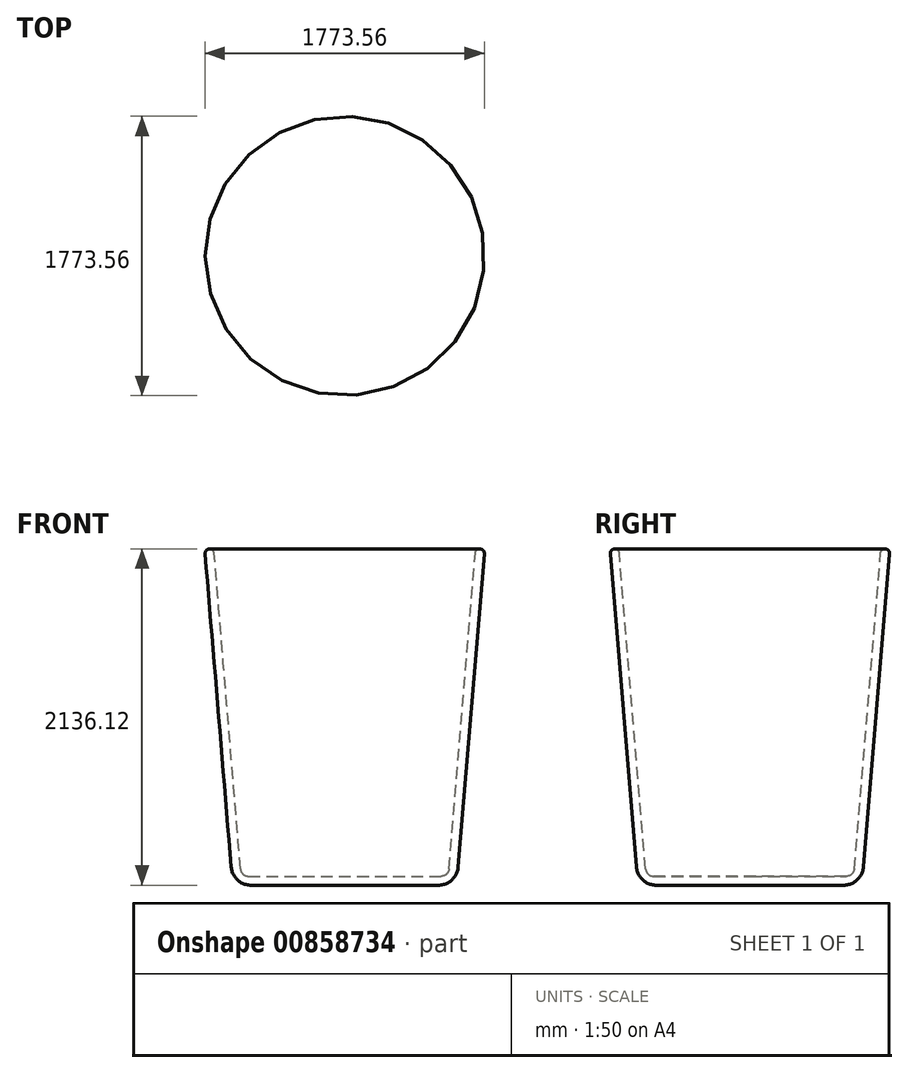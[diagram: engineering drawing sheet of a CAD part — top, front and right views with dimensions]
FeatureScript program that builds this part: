
annotation { "Feature Type Name" : "Feature", "Feature Type Description" : "" }
export const myFeature = defineFeature(function(context is Context, id is Id, definition is map)
    precondition{}
    {
        {
            var Q0;
            Q0=qCreatedBy(makeId("Front.planeOp"),FACE);
            var sketch = newSketch(context, id + "F0", { "sketchPlane" : qUnion([Q0])});
            skLineSegment(sketch, "E0", {"start": v(116.86, 0) * mm, "end": v(711.2, 0) * mm});
            skLineSegment(sketch, "E1", {"start": v(-9.7, 116.45) * mm, "end": v(-175.48, 2105.76) * mm});
            skLineSegment(sketch, "E2", {"start": v(711.2, 0) * mm, "end": v(711.2, 2133.6) * mm});
            skLineSegment(sketch, "E3.0", {"start": v(48.7, 103.73) * mm, "end": v(-118.53, 2110.5) * mm});
            skLineSegment(sketch, "E3.1", {"start": v(99.33, 57.15) * mm, "end": v(711.2, 57.15) * mm});
            skPoint(sketch, "E4.visualSharp", {"position": v(52.59, 57.15) * mm});
            skArc(sketch, "E4.filletArc", {"start": v(48.7, 103.73) * mm, "mid": v(64.93, 70.57) * mm, "end": v(99.33, 57.15) * mm});
            skPoint(sketch, "E5.visualSharp", {"position": v(0, 0) * mm});
            skArc(sketch, "E5.filletArc", {"start": v(-9.7, 116.45) * mm, "mid": v(30.86, 33.54) * mm, "end": v(116.86, 0) * mm});
            skLineSegment(sketch, "E6", {"start": v(-149.96, 2135.92) * mm, "end": v(-148.7, 2136.03) * mm});
            skPoint(sketch, "E7.visualSharp", {"position": v(-177.8, 2133.6) * mm});
            skArc(sketch, "E7.filletArc", {"start": v(-149.96, 2135.92) * mm, "mid": v(-168.97, 2126.12) * mm, "end": v(-175.48, 2105.76) * mm});
            skPoint(sketch, "E8.visualSharp", {"position": v(-120.85, 2138.35) * mm});
            skArc(sketch, "E8.filletArc", {"start": v(-118.53, 2110.5) * mm, "mid": v(-128.32, 2129.51) * mm, "end": v(-148.7, 2136.03) * mm});
            skSolve(sketch);
        }
        {
            var Q0;
            Q0=qSketchRegion(id+"F0",true);
            var Q1;
            Q1=sQuery(id+"F0.wireOp",EDGE,"E2");
            revolve(context, id + "F1", {"surfaceOperationType" : NewSurfaceOperationType.NEW, "entities" : qUnion([Q0]), "axis" : qUnion([Q1]), "revolveType" : RevolveType.FULL});
        }
    });
